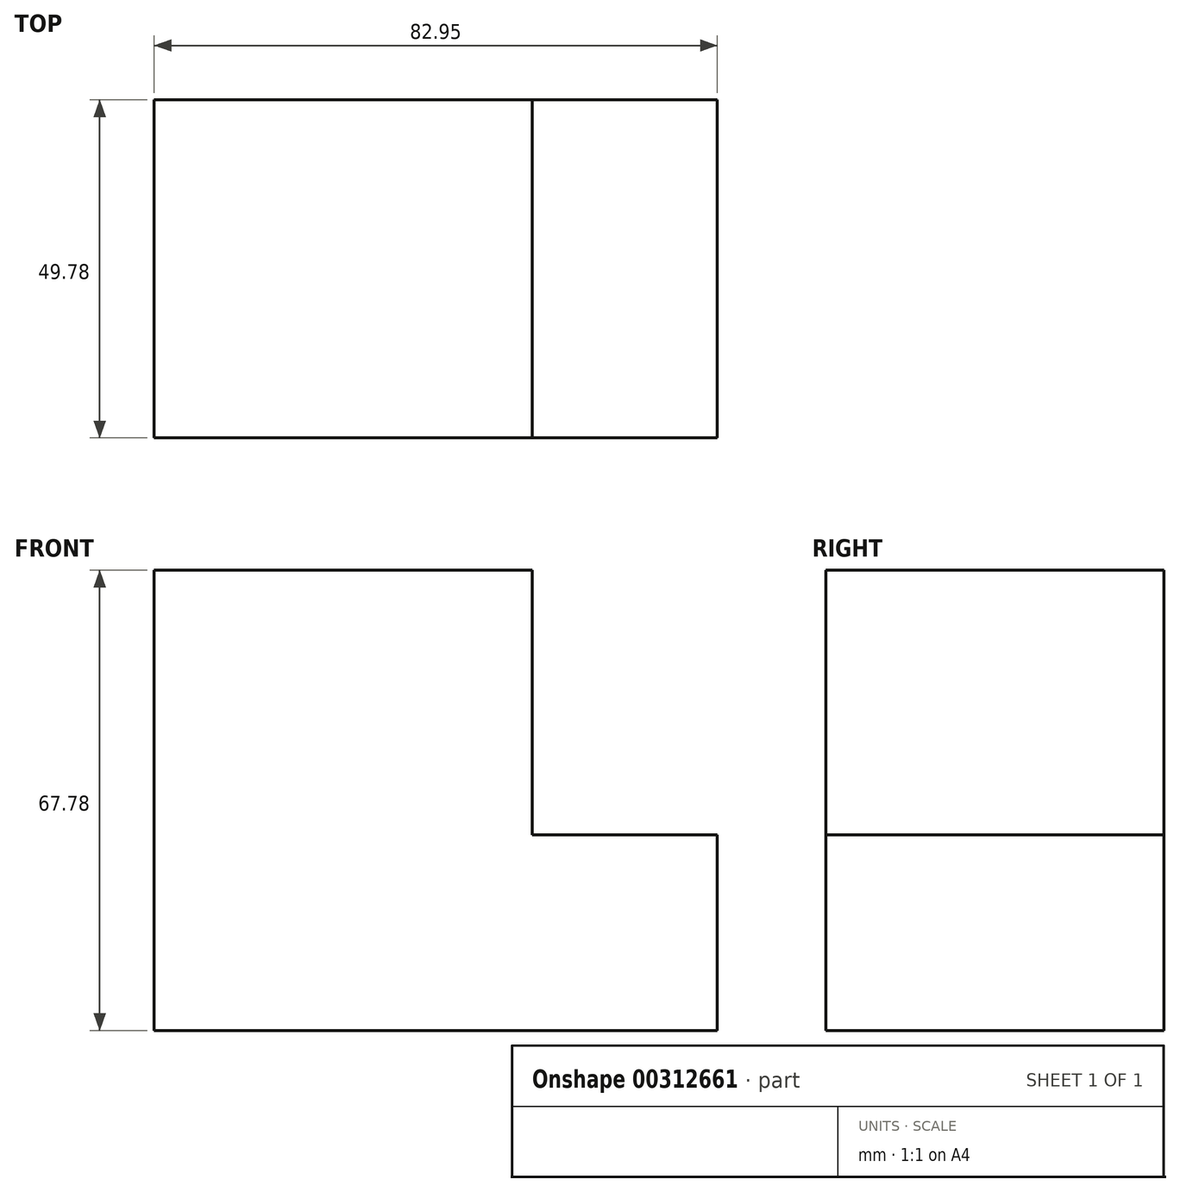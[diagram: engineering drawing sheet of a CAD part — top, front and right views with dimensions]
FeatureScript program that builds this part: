
annotation { "Feature Type Name" : "Feature", "Feature Type Description" : "" }
export const myFeature = defineFeature(function(context is Context, id is Id, definition is map)
    precondition{}
    {
        {
            var Q0;
            Q0=qCreatedBy(makeId("Front.planeOp"),FACE);
            var sketch = newSketch(context, id + "F0", { "sketchPlane" : qUnion([Q0])});
            skLineSegment(sketch, "E0", {"start": v(33.74, -38.53) * mm, "end": v(33.74, -9.75) * mm});
            skLineSegment(sketch, "E1", {"start": v(33.74, -9.75) * mm, "end": v(6.5, -9.75) * mm});
            skLineSegment(sketch, "E2", {"start": v(6.5, -9.75) * mm, "end": v(6.5, 29.25) * mm});
            skLineSegment(sketch, "E3", {"start": v(6.5, 29.25) * mm, "end": v(-49.21, 29.25) * mm});
            skLineSegment(sketch, "E4", {"start": v(-49.21, 29.25) * mm, "end": v(-49.21, -38.53) * mm});
            skLineSegment(sketch, "E5", {"start": v(-49.21, -38.53) * mm, "end": v(33.74, -38.53) * mm});
            skSolve(sketch);
        }
        {
            var Q0;
            Q0=makeQuery(id+"F0.imprint","IMPRINT",FACE,{"disambiguationData":[TD([[makeQuery(id+"F0.imprint","IMPRINT",EDGE,{"derivedFrom":sQuery(id+"F0.wireOp",EDGE,"E0")}),1.0]])]});
            extrude(context, id + "F1", {"entities" : qUnion([Q0]), "depth" : 49.78 * mm});
        }
    });
